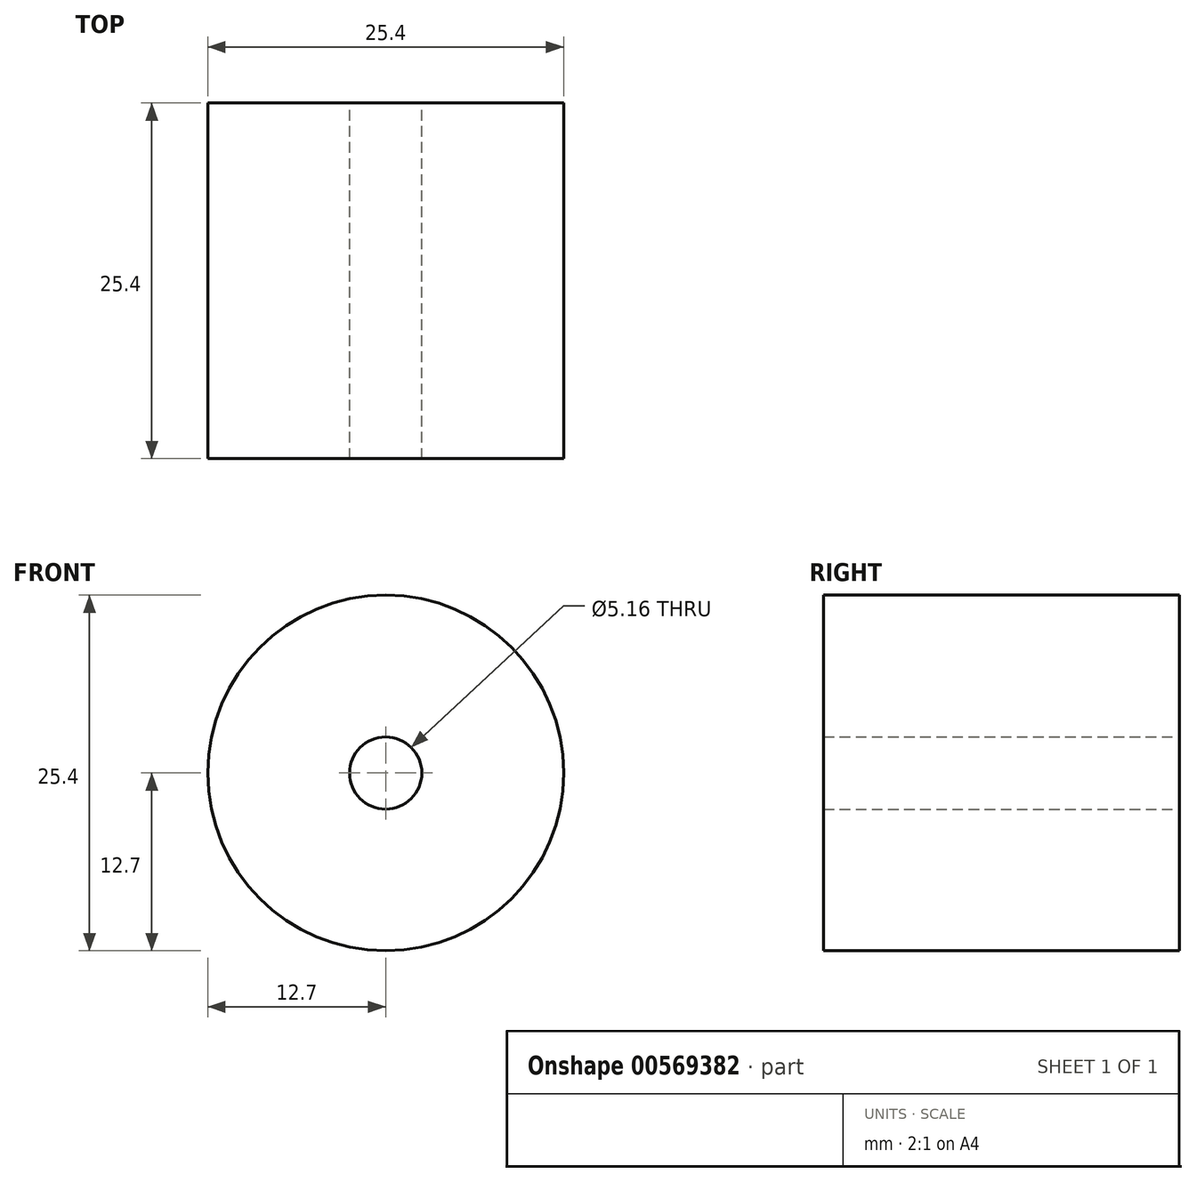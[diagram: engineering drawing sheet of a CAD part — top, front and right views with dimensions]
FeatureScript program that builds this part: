
annotation { "Feature Type Name" : "Feature", "Feature Type Description" : "" }
export const myFeature = defineFeature(function(context is Context, id is Id, definition is map)
    precondition{}
    {
        {
            var Q0;
            Q0=qCreatedBy(makeId("Front.planeOp"),FACE);
            var sketch = newSketch(context, id + "F0", { "sketchPlane" : qUnion([Q0])});
            skCircle(sketch, "E0", {"center": v(0, 0) * mm, "radius": 12.7 * mm});
            skCircle(sketch, "E1", {"center": v(0, 0) * mm, "radius": 2.58 * mm});
            skSolve(sketch);
        }
        {
            var Q0;
            Q0=makeQuery(id+"F0.imprint","IMPRINT",FACE,{"disambiguationData":[TD([[makeQuery(id+"F0.imprint","IMPRINT",EDGE,{"derivedFrom":sQuery(id+"F0.wireOp",EDGE,"E0")}),1.0]])]});
            var sketch = newSketch(context, id + "F1", { "sketchPlane" : qUnion([Q0])});
            skSolve(sketch);
        }
        {
            var Q0;
            Q0 = qSketchRegion(id + "F1", true);
            var Q1;
            Q1=makeQuery(id+"F0.imprint","IMPRINT",FACE,{"disambiguationData":[TD([[makeQuery(id+"F0.imprint","IMPRINT",EDGE,{"derivedFrom":sQuery(id+"F0.wireOp",EDGE,"E0")}),1.0]])]});
            extrude(context, id + "F2", {"entities" : qUnion([Q0, Q1]), "depth" : 25.4 * mm, "offsetDistance" : 25.4 * mm});
        }
    });
